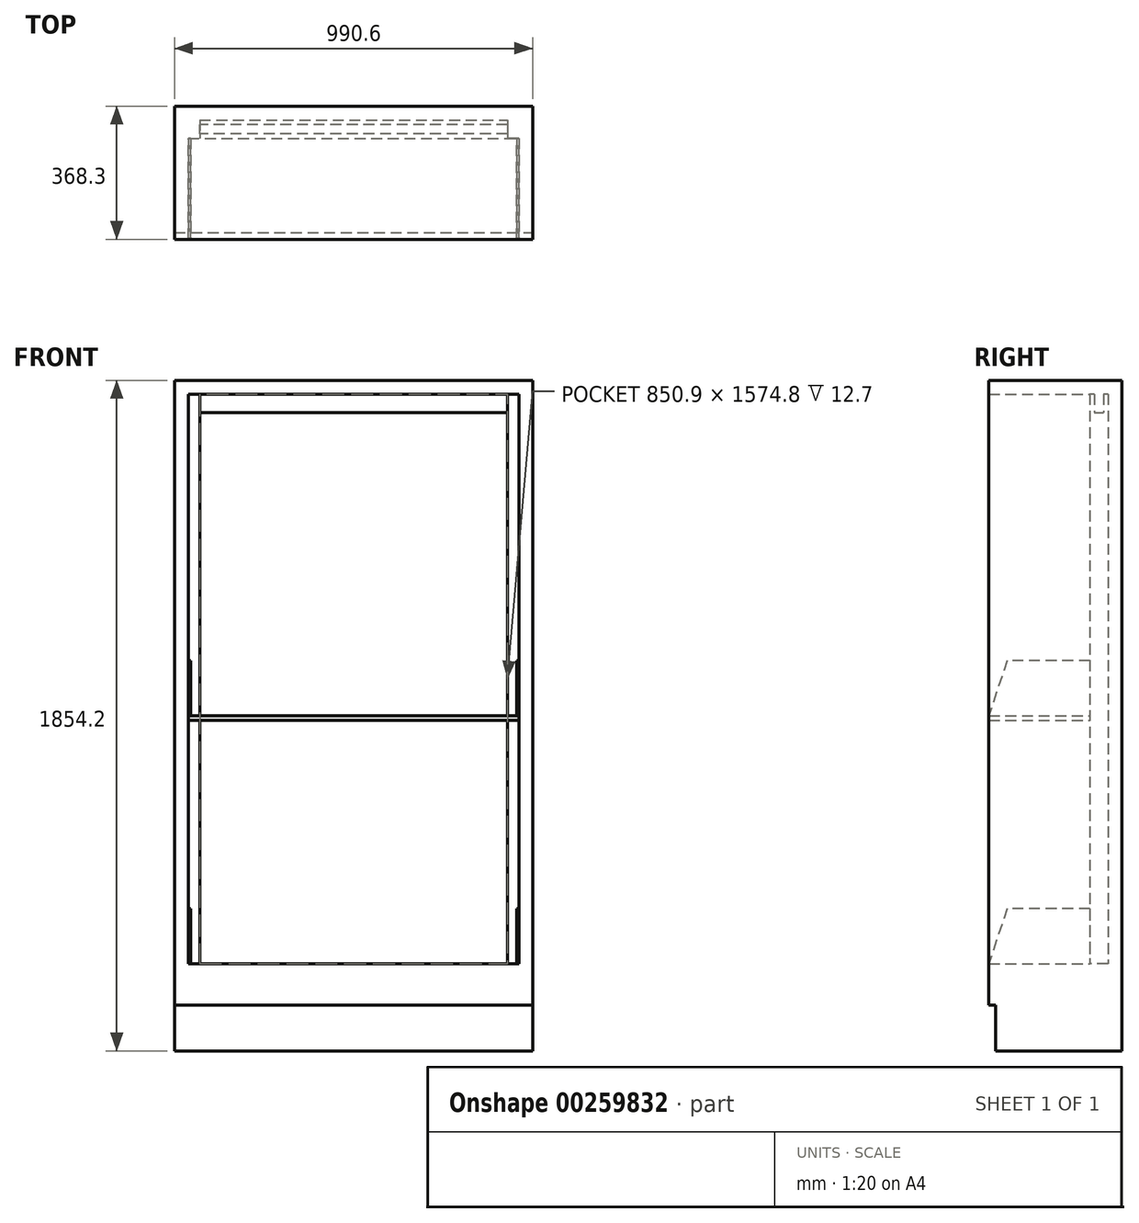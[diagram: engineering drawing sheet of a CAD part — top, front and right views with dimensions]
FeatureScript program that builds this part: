
annotation { "Feature Type Name" : "Feature", "Feature Type Description" : "" }
export const myFeature = defineFeature(function(context is Context, id is Id, definition is map)
    precondition{}
    {
        {
            var Q0;
            Q0=qCreatedBy(makeId("Front.planeOp"),FACE);
            var sketch = newSketch(context, id + "F0", { "sketchPlane" : qUnion([Q0])});
            skLineSegment(sketch, "E0.bottom", {"start": v(-495.3, 0) * mm, "end": v(495.3, 0) * mm});
            skLineSegment(sketch, "E0.top", {"start": v(-495.3, 127) * mm, "end": v(495.3, 127) * mm});
            skLineSegment(sketch, "E0.left", {"start": v(-495.3, 0) * mm, "end": v(-495.3, 127) * mm});
            skLineSegment(sketch, "E0.right", {"start": v(495.3, 0) * mm, "end": v(495.3, 127) * mm});
            skSolve(sketch);
        }
        {
            var Q0;
            Q0 = qSketchRegion(id + "F0", true);
            extrude(context, id + "F1", {"entities" : qUnion([Q0]), "depth" : 304.8 * mm + 6.35 * mm});
        }
        {
            var Q0;
            Q0=qCreatedBy(makeId("Front.planeOp"),FACE);
            var sketch = newSketch(context, id + "F2", { "sketchPlane" : qUnion([Q0])});
            skLineSegment(sketch, "E1.0", {"start": v(-495.3, 127) * mm, "end": v(495.3, 127) * mm});
            skLineSegment(sketch, "E2.top", {"start": v(-495.3, 1854.2) * mm, "end": v(495.3, 1854.2) * mm});
            skLineSegment(sketch, "E2.left", {"start": v(-495.3, 127) * mm, "end": v(-495.3, 1854.2) * mm});
            skLineSegment(sketch, "E2.right", {"start": v(495.3, 127) * mm, "end": v(495.3, 1854.2) * mm});
            skLineSegment(sketch, "E3.bottom", {"start": v(-457.2, 1816.1) * mm, "end": v(457.2, 1816.1) * mm});
            skLineSegment(sketch, "E3.top", {"start": v(-457.2, 165.1) * mm, "end": v(457.2, 165.1) * mm});
            skLineSegment(sketch, "E3.left", {"start": v(-457.2, 1816.1) * mm, "end": v(-457.2, 165.1) * mm});
            skLineSegment(sketch, "E3.right", {"start": v(457.2, 1816.1) * mm, "end": v(457.2, 165.1) * mm});
            skSolve(sketch);
        }
        {
            var Q0;
            Q0 = qSketchRegion(id + "F2", true);
            extrude(context, id + "F3", {"entities" : qUnion([Q0]), "operationType" : NewBodyOperationType.ADD, "depth" : 330.2 * mm});
        }
        {
            var Q0;
            Q0=makeQuery(id+"F3.boolean.opBoolean","MERGE",FACE,{"derivedFrom":[makeQuery(id+"F1.opExtrude","CAP_FACE",FACE,{"disambiguationData":[OSD([sQuery(id+"F0.wireOp",EDGE,"E0.bottom"),sQuery(id+"F0.wireOp",EDGE,"E0.top"),sQuery(id+"F0.wireOp",EDGE,"E0.left"),sQuery(id+"F0.wireOp",EDGE,"E0.right")])],"isStart":true}),makeQuery(id+"F3.opExtrude","CAP_FACE",FACE,{"disambiguationData":[OSD([sQuery(id+"F2.wireOp",EDGE,"E1.0"),sQuery(id+"F2.wireOp",EDGE,"E2.top"),sQuery(id+"F2.wireOp",EDGE,"E2.left"),sQuery(id+"F2.wireOp",EDGE,"E2.right"),sQuery(id+"F2.wireOp",EDGE,"E3.bottom"),sQuery(id+"F2.wireOp",EDGE,"E3.top"),sQuery(id+"F2.wireOp",EDGE,"E3.left"),sQuery(id+"F2.wireOp",EDGE,"E3.right")])],"isStart":true})]});
            var sketch = newSketch(context, id + "F4", { "sketchPlane" : qUnion([Q0])});
            skLineSegment(sketch, "E4.bottom", {"start": v(-495.3, 1854.2) * mm, "end": v(495.3, 1854.2) * mm});
            skLineSegment(sketch, "E4.top", {"start": v(-495.3, 0) * mm, "end": v(495.3, 0) * mm});
            skLineSegment(sketch, "E4.left", {"start": v(-495.3, 1854.2) * mm, "end": v(-495.3, 0) * mm});
            skLineSegment(sketch, "E4.right", {"start": v(495.3, 1854.2) * mm, "end": v(495.3, 0) * mm});
            skSolve(sketch);
        }
        {
            var Q0;
            Q0 = qSketchRegion(id + "F4", true);
            extrude(context, id + "F5", {"entities" : qUnion([Q0]), "operationType" : NewBodyOperationType.ADD, "depth" : 38.1 * mm});
        }
        {
            var Q0;
            Q0=makeQuery(id+"F3.opExtrude","SWEPT_FACE",FACE,{"disambiguationData":[OSD([sQuery(id+"F2.wireOp",EDGE,"E3.top")])]});
            var sketch = newSketch(context, id + "F6", { "sketchPlane" : qUnion([Q0])});
            skLineSegment(sketch, "E5.bottom", {"start": v(-457.2, 0) * mm, "end": v(-425.45, 0) * mm});
            skLineSegment(sketch, "E5.top", {"start": v(-457.2, -50.8) * mm, "end": v(-425.45, -50.8) * mm});
            skLineSegment(sketch, "E5.left", {"start": v(-457.2, 0) * mm, "end": v(-457.2, -50.8) * mm});
            skLineSegment(sketch, "E5.right", {"start": v(-425.45, 0) * mm, "end": v(-425.45, -50.8) * mm});
            skLineSegment(sketch, "E6.bottom", {"start": v(457.2, 0) * mm, "end": v(425.45, 0) * mm});
            skLineSegment(sketch, "E6.top", {"start": v(457.2, -50.8) * mm, "end": v(425.45, -50.8) * mm});
            skLineSegment(sketch, "E6.left", {"start": v(457.2, 0) * mm, "end": v(457.2, -50.8) * mm});
            skLineSegment(sketch, "E6.right", {"start": v(425.45, 0) * mm, "end": v(425.45, -50.8) * mm});
            skSolve(sketch);
        }
        {
            var Q0;
            Q0 = qSketchRegion(id + "F6", true);
            extrude(context, id + "F7", {"entities" : qUnion([Q0]), "depth" : 1651 * mm});
        }
        {
            var Q0;
            Q0=makeQuery(id+"F7.opExtrude","SWEPT_FACE",FACE,{"disambiguationData":[OSD([sQuery(id+"F6.wireOp",EDGE,"E5.right")])]});
            var sketch = newSketch(context, id + "F8", { "sketchPlane" : qUnion([Q0])});
            skLineSegment(sketch, "E7.bottom", {"start": v(-38.1, 1816.1) * mm, "end": v(-12.7, 1816.1) * mm});
            skLineSegment(sketch, "E7.top", {"start": v(-38.1, 1765.3) * mm, "end": v(-12.7, 1765.3) * mm});
            skLineSegment(sketch, "E7.left", {"start": v(-38.1, 1816.1) * mm, "end": v(-38.1, 1765.3) * mm});
            skLineSegment(sketch, "E7.right", {"start": v(-12.7, 1816.1) * mm, "end": v(-12.7, 1765.3) * mm});
            skSolve(sketch);
        }
        {
            var Q0;
            Q0 = qSketchRegion(id + "F8", true);
            extrude(context, id + "F9", {"entities" : qUnion([Q0]), "operationType" : NewBodyOperationType.ADD, "depth" : 863.6 * mm});
        }
        {
            var Q0;
            Q0=makeQuery(id+"F3.opExtrude","SWEPT_FACE",FACE,{"disambiguationData":[OSD([sQuery(id+"F2.wireOp",EDGE,"E3.top")])]});
            var sketch = newSketch(context, id + "F10", { "sketchPlane" : qUnion([Q0])});
            skLineSegment(sketch, "E8.bottom", {"start": v(-457.2, -330.2) * mm, "end": v(457.2, -330.2) * mm});
            skLineSegment(sketch, "E8.top", {"start": v(-457.2, 0) * mm, "end": v(457.2, 0) * mm});
            skLineSegment(sketch, "E8.left", {"start": v(-457.2, -330.2) * mm, "end": v(-457.2, 0) * mm});
            skLineSegment(sketch, "E8.right", {"start": v(457.2, -330.2) * mm, "end": v(457.2, 0) * mm});
            skSolve(sketch);
        }
        {
            var Q0;
            Q0 = qSketchRegion(id + "F10", true);
            extrude(context, id + "F11", {"entities" : qUnion([Q0]), "operationType" : NewBodyOperationType.ADD, "depth" : 76.2 * mm});
        }
        {
            var Q0;
            Q0=makeQuery(id+"F3.opExtrude","SWEPT_FACE",FACE,{"disambiguationData":[OSD([sQuery(id+"F2.wireOp",EDGE,"E3.left")])]});
            var sketch = newSketch(context, id + "F12", { "sketchPlane" : qUnion([Q0])});
            skPoint(sketch, "E9.0", {"position": v(-50.8, 241.3) * mm});
            skLineSegment(sketch, "E10", {"start": v(-50.8, 241.3) * mm, "end": v(-50.8, 393.7) * mm});
            skLineSegment(sketch, "E11", {"start": v(-50.8, 393.7) * mm, "end": v(-279.4, 393.7) * mm});
            skLineSegment(sketch, "E12", {"start": v(-279.4, 393.7) * mm, "end": v(-330.2, 241.3) * mm});
            skLineSegment(sketch, "E13", {"start": v(-330.2, 241.3) * mm, "end": v(-50.8, 241.3) * mm});
            skSolve(sketch);
        }
        {
            var Q0;
            Q0 = qSketchRegion(id + "F12", true);
            extrude(context, id + "F13", {"entities" : qUnion([Q0]), "depth" : 6.35 * mm});
        }
        {
            var Q0;
            Q0=makeQuery(id+"F13.opExtrude","SWEPT_BODY",BODY,{"disambiguationData":[OSD([sQuery(id+"F12.wireOp",EDGE,"E10"),sQuery(id+"F12.wireOp",EDGE,"E11"),sQuery(id+"F12.wireOp",EDGE,"E12"),sQuery(id+"F12.wireOp",EDGE,"E13")])]});
            var Q1;
            Q1=qCreatedBy(makeId("Right.planeOp"),FACE);
            mirror(context, id + "F14", {"entities" : qUnion([Q0]), "mirrorPlane" : qUnion([Q1])});
        }
        {
            var Q0;
            Q0=makeQuery(id+"F14.opPattern","COPY",BODY,{"derivedFrom":makeQuery(id+"F13.opExtrude","SWEPT_BODY",BODY,{"disambiguationData":[OSD([sQuery(id+"F12.wireOp",EDGE,"E10"),sQuery(id+"F12.wireOp",EDGE,"E11"),sQuery(id+"F12.wireOp",EDGE,"E12"),sQuery(id+"F12.wireOp",EDGE,"E13")])]}),"instanceName":"1"});
            var Q1;
            Q1=makeQuery(id+"F7.opExtrude","SWEPT_BODY",BODY,{"disambiguationData":[OSD([sQuery(id+"F6.wireOp",EDGE,"E5.bottom"),sQuery(id+"F6.wireOp",EDGE,"E5.top"),sQuery(id+"F6.wireOp",EDGE,"E5.left"),sQuery(id+"F6.wireOp",EDGE,"E5.right")])]});
            var Q2;
            Q2=makeQuery(id+"F13.opExtrude","SWEPT_BODY",BODY,{"disambiguationData":[OSD([sQuery(id+"F12.wireOp",EDGE,"E10"),sQuery(id+"F12.wireOp",EDGE,"E11"),sQuery(id+"F12.wireOp",EDGE,"E12"),sQuery(id+"F12.wireOp",EDGE,"E13")])]});
            booleanBodies(context, id + "F15", {"operationType" : BooleanOperationType.UNION, "tools" : qUnion([Q0, Q1, Q2])});
        }
        {
            var Q0;
            Q0=qCreatedBy(makeId("Top.planeOp"),FACE);
            cPlane(context, id + "F16", {"entities" : qUnion([Q0]), "cplaneType" : CPlaneType.OFFSET, "offset" : 914.4 * mm, "width" : 152.4 * mm, "height" : 152.4 * mm});
        }
        {
            var Q0;
            Q0=qCreatedBy(id+"F16.planeOp",FACE);
            var sketch = newSketch(context, id + "F17", { "sketchPlane" : qUnion([Q0])});
            skLineSegment(sketch, "E14.0.0", {"start": v(-450.85, -330.2) * mm, "end": v(450.85, -330.2) * mm, "construction": true});
            skLineSegment(sketch, "E14.0.1", {"start": v(450.85, -330.2) * mm, "end": v(450.85, -50.8) * mm, "construction": true});
            skLineSegment(sketch, "E14.0.2", {"start": v(450.85, -50.8) * mm, "end": v(425.45, -50.8) * mm, "construction": true});
            skLineSegment(sketch, "E14.0.3", {"start": v(425.45, -50.8) * mm, "end": v(425.45, 0) * mm, "construction": true});
            skLineSegment(sketch, "E14.0.4", {"start": v(425.45, 0) * mm, "end": v(-425.45, 0) * mm, "construction": true});
            skLineSegment(sketch, "E14.0.5", {"start": v(-425.45, 0) * mm, "end": v(-425.45, -50.8) * mm, "construction": true});
            skLineSegment(sketch, "E14.0.6", {"start": v(-425.45, -50.8) * mm, "end": v(-450.85, -50.8) * mm, "construction": true});
            skLineSegment(sketch, "E14.0.7", {"start": v(-450.85, -50.8) * mm, "end": v(-450.85, -330.2) * mm, "construction": true});
            skLineSegment(sketch, "E15.0", {"start": v(-457.2, -330.2) * mm, "end": v(457.2, -330.2) * mm, "construction": true});
            skLineSegment(sketch, "E16.bottom", {"start": v(-457.2, -330.2) * mm, "end": v(457.2, -330.2) * mm});
            skLineSegment(sketch, "E16.top", {"start": v(-457.2, -50.8) * mm, "end": v(457.2, -50.8) * mm});
            skLineSegment(sketch, "E16.left", {"start": v(-457.2, -330.2) * mm, "end": v(-457.2, -50.8) * mm});
            skLineSegment(sketch, "E16.right", {"start": v(457.2, -330.2) * mm, "end": v(457.2, -50.8) * mm});
            skSolve(sketch);
        }
        {
            var Q0;
            Q0 = qSketchRegion(id + "F17", true);
            extrude(context, id + "F18", {"entities" : qUnion([Q0]), "depth" : 12.7 * mm});
        }
        {
            var Q0;
            Q0=makeQuery(id+"F3.opExtrude","SWEPT_FACE",FACE,{"disambiguationData":[OSD([sQuery(id+"F2.wireOp",EDGE,"E3.left")])]});
            var sketch = newSketch(context, id + "F19", { "sketchPlane" : qUnion([Q0])});
            skLineSegment(sketch, "E17.0", {"start": v(-50.8, 1816.1) * mm, "end": v(-50.8, 393.7) * mm});
            skLineSegment(sketch, "E18.0", {"start": v(-330.2, 927.1) * mm, "end": v(-50.8, 927.1) * mm});
            skLineSegment(sketch, "E19", {"start": v(-50.8, 1079.5) * mm, "end": v(-279.4, 1079.5) * mm});
            skLineSegment(sketch, "E20", {"start": v(-279.4, 1079.5) * mm, "end": v(-330.2, 927.1) * mm});
            skSolve(sketch);
        }
        {
            var Q0;
            Q0 = qSketchRegion(id + "F19", true);
            extrude(context, id + "F20", {"entities" : qUnion([Q0]), "depth" : 6.35 * mm});
        }
        {
            var Q0;
            Q0=makeQuery(id+"F20.opExtrude","SWEPT_BODY",BODY,{"disambiguationData":[OSD([sQuery(id+"F19.wireOp",EDGE,"E17.0"),sQuery(id+"F19.wireOp",EDGE,"E18.0"),sQuery(id+"F19.wireOp",EDGE,"E19"),sQuery(id+"F19.wireOp",EDGE,"E20")])]});
            var Q1;
            Q1=qCreatedBy(makeId("Right.planeOp"),FACE);
            mirror(context, id + "F21", {"entities" : qUnion([Q0]), "mirrorPlane" : qUnion([Q1])});
        }
    });
